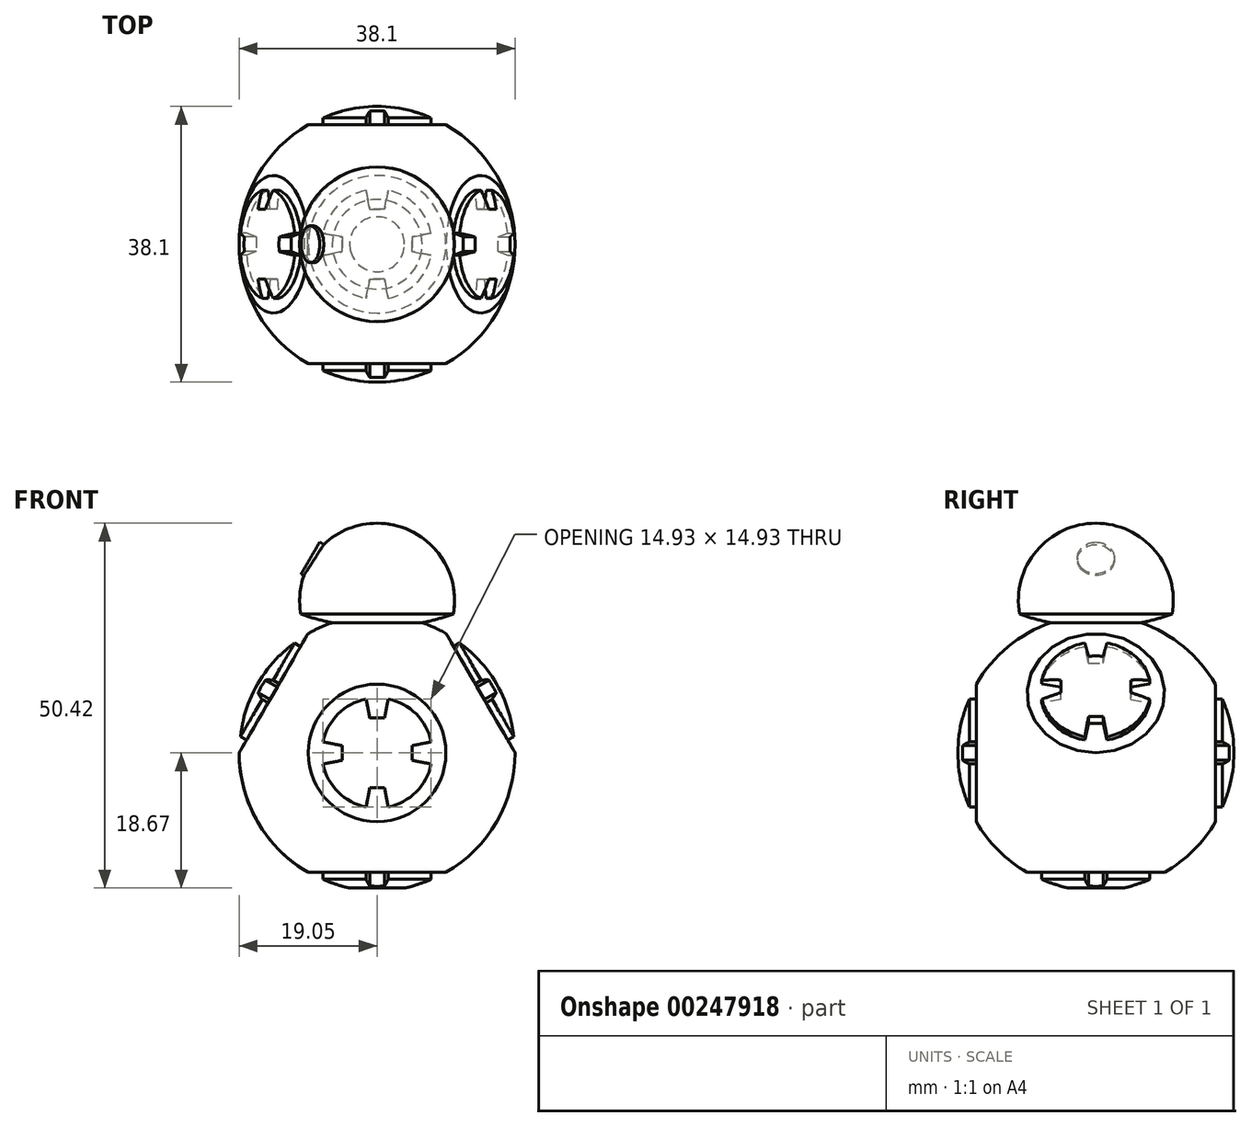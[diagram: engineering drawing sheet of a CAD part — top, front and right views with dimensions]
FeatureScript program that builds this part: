
annotation { "Feature Type Name" : "Feature", "Feature Type Description" : "" }
export const myFeature = defineFeature(function(context is Context, id is Id, definition is map)
    precondition{}
    {
        {
            var Q0;
            Q0=qCreatedBy(makeId("Front.planeOp"),FACE);
            var sketch = newSketch(context, id + "F0", { "sketchPlane" : qUnion([Q0])});
            skArc(sketch, "E0", {"start": v(-6.2, 18.01) * mm, "mid": v(-18.79, -3.15) * mm, "end": v(0, -19.05) * mm});
            skLineSegment(sketch, "E1", {"start": v(0, -19.05) * mm, "end": v(0, 31.75) * mm});
            skArc(sketch, "E2", {"start": v(-10.54, 19.2) * mm, "mid": v(-8.4, 18.52) * mm, "end": v(-6.2, 18.01) * mm});
            skArc(sketch, "E3.trimOffspring", {"start": v(0, 31.75) * mm, "mid": v(-8.2, 27.93) * mm, "end": v(-10.54, 19.2) * mm});
            skPoint(sketch, "E4.trimOffspring.end.orphan", {"position": v(9.8, 19.2) * mm});
            skPoint(sketch, "E5", {"position": v(-17, -8.58) * mm});
            skLineSegment(sketch, "E6", {"start": v(-6, 29.9) * mm, "end": v(-10.66, 21.92) * mm, "construction": true});
            skSolve(sketch);
        }
        {
            var Q0;
            {var subQ0=sQuery(id+"F0.wireOp",EDGE,"E0");Q0=makeQuery(id+"F0.imprint","IMPRINT",FACE,{"disambiguationData":[TD([[makeQuery(id+"F0.imprint","IMPRINT",EDGE,{"derivedFrom":subQ0}),1.0]])]});}
            var Q1;
            Q1=sQuery(id+"F0.wireOp",EDGE,"E1");
            revolve(context, id + "F1", {"entities" : qUnion([Q0]), "axis" : qUnion([Q1]), "revolveType" : RevolveType.FULL});
        }
        {
            var Q0;
            Q0=qCreatedBy(makeId("Front.planeOp"),FACE);
            cPlane(context, id + "F2", {"entities" : qUnion([Q0]), "cplaneType" : CPlaneType.OFFSET, "offset" : 19.05 * mm, "width" : 152.4 * mm, "height" : 152.4 * mm});
        }
        {
            var Q0;
            Q0=qCreatedBy(id+"F2.planeOp",FACE);
            var sketch = newSketch(context, id + "F3", { "sketchPlane" : qUnion([Q0])});
            skCircle(sketch, "E7", {"center": v(0, 0) * mm, "radius": 10.67 * mm});
            skArc(sketch, "E8", {"start": v(1.53, -7.47) * mm, "mid": v(5.39, -5.39) * mm, "end": v(7.47, -1.53) * mm});
            skLineSegment(sketch, "E9", {"start": v(0, -4.83) * mm, "end": v(-1.02, -4.83) * mm});
            skLineSegment(sketch, "E10", {"start": v(-1.02, -4.83) * mm, "end": v(-1.53, -7.47) * mm});
            skLineSegment(sketch, "E11.MirrorCS", {"start": v(1.02, -4.83) * mm, "end": v(1.53, -7.47) * mm});
            skLineSegment(sketch, "E12.MirrorCS", {"start": v(0, -4.83) * mm, "end": v(1.02, -4.83) * mm});
            skLineSegment(sketch, "E13.1.0", {"start": v(4.83, -1.02) * mm, "end": v(7.47, -1.53) * mm});
            skLineSegment(sketch, "E13.1.1", {"start": v(4.83, 0) * mm, "end": v(4.83, 1.02) * mm});
            skLineSegment(sketch, "E13.1.2", {"start": v(4.83, 0) * mm, "end": v(4.83, -1.02) * mm});
            skLineSegment(sketch, "E13.1.3", {"start": v(4.83, 1.02) * mm, "end": v(7.47, 1.53) * mm});
            skLineSegment(sketch, "E13.2.0", {"start": v(1.02, 4.83) * mm, "end": v(1.53, 7.47) * mm});
            skLineSegment(sketch, "E13.2.1", {"start": v(0, 4.83) * mm, "end": v(-1.02, 4.83) * mm});
            skLineSegment(sketch, "E13.2.2", {"start": v(0, 4.83) * mm, "end": v(1.02, 4.83) * mm});
            skLineSegment(sketch, "E13.2.3", {"start": v(-1.02, 4.83) * mm, "end": v(-1.53, 7.47) * mm});
            skLineSegment(sketch, "E13.3.0", {"start": v(-4.83, 1.02) * mm, "end": v(-7.47, 1.53) * mm});
            skLineSegment(sketch, "E13.3.1", {"start": v(-4.83, 0) * mm, "end": v(-4.83, -1.02) * mm});
            skLineSegment(sketch, "E13.3.2", {"start": v(-4.83, 0) * mm, "end": v(-4.83, 1.02) * mm});
            skLineSegment(sketch, "E13.3.3", {"start": v(-4.83, -1.02) * mm, "end": v(-7.47, -1.53) * mm});
            skArc(sketch, "E14.trimOffspring", {"start": v(-7.47, -1.53) * mm, "mid": v(-5.39, -5.39) * mm, "end": v(-1.53, -7.47) * mm});
            skArc(sketch, "E15.trimOffspring", {"start": v(-1.53, 7.47) * mm, "mid": v(-5.39, 5.39) * mm, "end": v(-7.47, 1.53) * mm});
            skArc(sketch, "E16.trimOffspring", {"start": v(7.47, 1.53) * mm, "mid": v(5.39, 5.39) * mm, "end": v(1.53, 7.47) * mm});
            skSolve(sketch);
        }
        {
            var Q0;
            Q0 = qSketchRegion(id + "F3", true);
            extrude(context, id + "F4", {"entities" : qUnion([Q0]), "operationType" : NewBodyOperationType.REMOVE, "oppositeDirection" : true, "depth" : 2.54 * mm});
        }
        {
            var Q0;
            Q0=qCreatedBy(makeId("Front.planeOp"),FACE);
            var sketch = newSketch(context, id + "F5", { "sketchPlane" : qUnion([Q0])});
            skCircle(sketch, "E17", {"center": v(0, 0) * mm, "radius": 19.05 * mm});
            skLineSegment(sketch, "E18", {"start": v(0, -19.05) * mm, "end": v(0, 19.05) * mm});
            skLineSegment(sketch, "E19", {"start": v(0, 0) * mm, "end": v(0, 19.05) * mm});
            skLineSegment(sketch, "E20", {"start": v(0, 19.05) * mm, "end": v(16.5, -9.53) * mm});
            skLineSegment(sketch, "E21", {"start": v(16.5, -9.53) * mm, "end": v(0, -9.53) * mm});
            skLineSegment(sketch, "E22.MirrorCS", {"start": v(0, 19.05) * mm, "end": v(-16.5, -9.53) * mm});
            skLineSegment(sketch, "E23.MirrorCS", {"start": v(-16.5, -9.53) * mm, "end": v(0, -9.53) * mm});
            skLineSegment(sketch, "E24", {"start": v(16.5, 9.53) * mm, "end": v(25.5, -6.07) * mm});
            skLineSegment(sketch, "E25.MirrorCS", {"start": v(16.5, 9.52) * mm, "end": v(7.5, 25.12) * mm});
            skLineSegment(sketch, "E26.1.0", {"start": v(-16.5, 9.53) * mm, "end": v(-25.5, -6.07) * mm});
            skLineSegment(sketch, "E26.1.1", {"start": v(-16.5, 9.52) * mm, "end": v(-7.5, 25.12) * mm});
            skLineSegment(sketch, "E26.2.0", {"start": v(0, -19.05) * mm, "end": v(18, -19.05) * mm});
            skLineSegment(sketch, "E26.2.1", {"start": v(0, -19.05) * mm, "end": v(-18, -19.05) * mm});
            skPoint(sketch, "E27.start.orphan", {"position": v(8.25, 4.76) * mm});
            skLineSegment(sketch, "E28", {"start": v(0, 0) * mm, "end": v(-16.5, 9.53) * mm});
            skLineSegment(sketch, "E29", {"start": v(0, 0) * mm, "end": v(16.5, 9.53) * mm});
            skSolve(sketch);
        }
        {
            var Q0;
            Q0=sQuery(id+"F5.wireOp",VERTEX,"E26.2.0.start");
            var Q1;
            Q1=sQuery(id+"F5.wireOp",EDGE,"E18");
            cPlane(context, id + "F6", {"entities" : qUnion([Q0, Q1]), "cplaneType" : CPlaneType.LINE_POINT, "offset" : 25.4 * mm, "width" : 152.4 * mm, "height" : 152.4 * mm});
        }
        {
            var Q0;
            Q0=qCreatedBy(id+"F6.planeOp",FACE);
            var sketch = newSketch(context, id + "F7", { "sketchPlane" : qUnion([Q0])});
            skCircle(sketch, "E30", {"center": v(0, 0) * mm, "radius": 10.67 * mm});
            skArc(sketch, "E31", {"start": v(1.53, -7.47) * mm, "mid": v(5.39, -5.39) * mm, "end": v(7.47, -1.53) * mm});
            skLineSegment(sketch, "E32", {"start": v(0, -4.83) * mm, "end": v(-1.02, -4.83) * mm});
            skLineSegment(sketch, "E33", {"start": v(-1.02, -4.83) * mm, "end": v(-1.53, -7.47) * mm});
            skLineSegment(sketch, "E34.MirrorCS", {"start": v(1.02, -4.83) * mm, "end": v(1.53, -7.47) * mm});
            skLineSegment(sketch, "E35.MirrorCS", {"start": v(0, -4.83) * mm, "end": v(1.02, -4.83) * mm});
            skLineSegment(sketch, "E36.1.0", {"start": v(4.83, -1.02) * mm, "end": v(7.47, -1.53) * mm});
            skLineSegment(sketch, "E36.1.1", {"start": v(4.83, 0) * mm, "end": v(4.83, 1.02) * mm});
            skLineSegment(sketch, "E36.1.2", {"start": v(4.83, 0) * mm, "end": v(4.83, -1.02) * mm});
            skLineSegment(sketch, "E36.1.3", {"start": v(4.83, 1.02) * mm, "end": v(7.47, 1.53) * mm});
            skLineSegment(sketch, "E36.2.0", {"start": v(1.02, 4.83) * mm, "end": v(1.53, 7.47) * mm});
            skLineSegment(sketch, "E36.2.1", {"start": v(0, 4.83) * mm, "end": v(-1.02, 4.83) * mm});
            skLineSegment(sketch, "E36.2.2", {"start": v(0, 4.83) * mm, "end": v(1.02, 4.83) * mm});
            skLineSegment(sketch, "E36.2.3", {"start": v(-1.02, 4.83) * mm, "end": v(-1.53, 7.47) * mm});
            skLineSegment(sketch, "E36.3.0", {"start": v(-4.83, 1.02) * mm, "end": v(-7.47, 1.53) * mm});
            skLineSegment(sketch, "E36.3.1", {"start": v(-4.83, 0) * mm, "end": v(-4.83, -1.02) * mm});
            skLineSegment(sketch, "E36.3.2", {"start": v(-4.83, 0) * mm, "end": v(-4.83, 1.02) * mm});
            skLineSegment(sketch, "E36.3.3", {"start": v(-4.83, -1.02) * mm, "end": v(-7.47, -1.53) * mm});
            skArc(sketch, "E37.trimOffspring", {"start": v(-7.47, -1.53) * mm, "mid": v(-5.39, -5.39) * mm, "end": v(-1.53, -7.47) * mm});
            skArc(sketch, "E38.trimOffspring", {"start": v(-1.53, 7.47) * mm, "mid": v(-5.39, 5.39) * mm, "end": v(-7.47, 1.53) * mm});
            skArc(sketch, "E39.trimOffspring", {"start": v(7.47, 1.53) * mm, "mid": v(5.39, 5.39) * mm, "end": v(1.53, 7.47) * mm});
            skSolve(sketch);
        }
        {
            var Q0;
            Q0=makeQuery(id+"F7.imprint","IMPRINT",FACE,{"disambiguationData":[TD([[makeQuery(id+"F7.imprint","IMPRINT",EDGE,{"derivedFrom":sQuery(id+"F7.wireOp",EDGE,"E30")}),1.0]])]});
            extrude(context, id + "F8", {"entities" : qUnion([Q0]), "operationType" : NewBodyOperationType.REMOVE, "depth" : 2.54 * mm});
        }
        {
            var Q0;
            Q0=sQuery(id+"F5.wireOp",VERTEX,"E28.end");
            var Q1;
            Q1=sQuery(id+"F5.wireOp",EDGE,"E28");
            cPlane(context, id + "F9", {"entities" : qUnion([Q0, Q1]), "cplaneType" : CPlaneType.LINE_POINT, "offset" : 25.4 * mm, "width" : 152.4 * mm, "height" : 152.4 * mm});
        }
        {
            var Q0;
            Q0=qCreatedBy(id+"F9.planeOp",FACE);
            var sketch = newSketch(context, id + "F10", { "sketchPlane" : qUnion([Q0])});
            skCircle(sketch, "E40", {"center": v(0, 0) * mm, "radius": 10.67 * mm});
            skArc(sketch, "E41", {"start": v(1.53, -7.47) * mm, "mid": v(5.39, -5.39) * mm, "end": v(7.47, -1.53) * mm});
            skLineSegment(sketch, "E42", {"start": v(0, -4.83) * mm, "end": v(-1.02, -4.83) * mm});
            skLineSegment(sketch, "E43", {"start": v(-1.02, -4.83) * mm, "end": v(-1.53, -7.47) * mm});
            skLineSegment(sketch, "E44.MirrorCS", {"start": v(1.02, -4.83) * mm, "end": v(1.53, -7.47) * mm});
            skLineSegment(sketch, "E45.MirrorCS", {"start": v(0, -4.83) * mm, "end": v(1.02, -4.83) * mm});
            skLineSegment(sketch, "E46.1.0", {"start": v(4.83, -1.02) * mm, "end": v(7.47, -1.53) * mm});
            skLineSegment(sketch, "E46.1.1", {"start": v(4.83, 0) * mm, "end": v(4.83, 1.02) * mm});
            skLineSegment(sketch, "E46.1.2", {"start": v(4.83, 0) * mm, "end": v(4.83, -1.02) * mm});
            skLineSegment(sketch, "E46.1.3", {"start": v(4.83, 1.02) * mm, "end": v(7.47, 1.53) * mm});
            skLineSegment(sketch, "E46.2.0", {"start": v(1.02, 4.83) * mm, "end": v(1.53, 7.47) * mm});
            skLineSegment(sketch, "E46.2.1", {"start": v(0, 4.83) * mm, "end": v(-1.02, 4.83) * mm});
            skLineSegment(sketch, "E46.2.2", {"start": v(0, 4.83) * mm, "end": v(1.02, 4.83) * mm});
            skLineSegment(sketch, "E46.2.3", {"start": v(-1.02, 4.83) * mm, "end": v(-1.53, 7.47) * mm});
            skLineSegment(sketch, "E46.3.0", {"start": v(-4.83, 1.02) * mm, "end": v(-7.47, 1.53) * mm});
            skLineSegment(sketch, "E46.3.1", {"start": v(-4.83, 0) * mm, "end": v(-4.83, -1.02) * mm});
            skLineSegment(sketch, "E46.3.2", {"start": v(-4.83, 0) * mm, "end": v(-4.83, 1.02) * mm});
            skLineSegment(sketch, "E46.3.3", {"start": v(-4.83, -1.02) * mm, "end": v(-7.47, -1.53) * mm});
            skArc(sketch, "E47.trimOffspring", {"start": v(-7.47, -1.53) * mm, "mid": v(-5.39, -5.39) * mm, "end": v(-1.53, -7.47) * mm});
            skArc(sketch, "E48.trimOffspring", {"start": v(-1.53, 7.47) * mm, "mid": v(-5.39, 5.39) * mm, "end": v(-7.47, 1.53) * mm});
            skArc(sketch, "E49.trimOffspring", {"start": v(7.47, 1.53) * mm, "mid": v(5.39, 5.39) * mm, "end": v(1.53, 7.47) * mm});
            skSolve(sketch);
        }
        {
            var Q0;
            Q0=makeQuery(id+"F10.imprint","IMPRINT",FACE,{"disambiguationData":[TD([[makeQuery(id+"F10.imprint","IMPRINT",EDGE,{"derivedFrom":sQuery(id+"F10.wireOp",EDGE,"E40")}),1.0]])]});
            extrude(context, id + "F11", {"entities" : qUnion([Q0]), "operationType" : NewBodyOperationType.REMOVE, "oppositeDirection" : true, "depth" : 2.54 * mm});
        }
        {
            var Q0;
            Q0=sQuery(id+"F5.wireOp",VERTEX,"E29.end");
            var Q1;
            Q1=sQuery(id+"F5.wireOp",EDGE,"E29");
            cPlane(context, id + "F12", {"entities" : qUnion([Q0, Q1]), "cplaneType" : CPlaneType.LINE_POINT, "offset" : 25.4 * mm, "width" : 152.4 * mm, "height" : 152.4 * mm});
        }
        {
            var Q0;
            Q0=qCreatedBy(id+"F12.planeOp",FACE);
            var sketch = newSketch(context, id + "F13", { "sketchPlane" : qUnion([Q0])});
            skCircle(sketch, "E50", {"center": v(0, 0) * mm, "radius": 10.67 * mm});
            skArc(sketch, "E51", {"start": v(1.53, -7.47) * mm, "mid": v(5.39, -5.39) * mm, "end": v(7.47, -1.53) * mm});
            skLineSegment(sketch, "E52", {"start": v(0, -4.83) * mm, "end": v(-1.02, -4.83) * mm});
            skLineSegment(sketch, "E53", {"start": v(-1.02, -4.83) * mm, "end": v(-1.53, -7.47) * mm});
            skLineSegment(sketch, "E54.MirrorCS", {"start": v(1.02, -4.83) * mm, "end": v(1.53, -7.47) * mm});
            skLineSegment(sketch, "E55.MirrorCS", {"start": v(0, -4.83) * mm, "end": v(1.02, -4.83) * mm});
            skLineSegment(sketch, "E56.1.0", {"start": v(4.83, -1.02) * mm, "end": v(7.47, -1.53) * mm});
            skLineSegment(sketch, "E56.1.1", {"start": v(4.83, 0) * mm, "end": v(4.83, 1.02) * mm});
            skLineSegment(sketch, "E56.1.2", {"start": v(4.83, 0) * mm, "end": v(4.83, -1.02) * mm});
            skLineSegment(sketch, "E56.1.3", {"start": v(4.83, 1.02) * mm, "end": v(7.47, 1.53) * mm});
            skLineSegment(sketch, "E56.2.0", {"start": v(1.02, 4.83) * mm, "end": v(1.53, 7.47) * mm});
            skLineSegment(sketch, "E56.2.1", {"start": v(0, 4.83) * mm, "end": v(-1.02, 4.83) * mm});
            skLineSegment(sketch, "E56.2.2", {"start": v(0, 4.83) * mm, "end": v(1.02, 4.83) * mm});
            skLineSegment(sketch, "E56.2.3", {"start": v(-1.02, 4.83) * mm, "end": v(-1.53, 7.47) * mm});
            skLineSegment(sketch, "E56.3.0", {"start": v(-4.83, 1.02) * mm, "end": v(-7.47, 1.53) * mm});
            skLineSegment(sketch, "E56.3.1", {"start": v(-4.83, 0) * mm, "end": v(-4.83, -1.02) * mm});
            skLineSegment(sketch, "E56.3.2", {"start": v(-4.83, 0) * mm, "end": v(-4.83, 1.02) * mm});
            skLineSegment(sketch, "E56.3.3", {"start": v(-4.83, -1.02) * mm, "end": v(-7.47, -1.53) * mm});
            skArc(sketch, "E57.trimOffspring", {"start": v(-7.47, -1.53) * mm, "mid": v(-5.39, -5.39) * mm, "end": v(-1.53, -7.47) * mm});
            skArc(sketch, "E58.trimOffspring", {"start": v(-1.53, 7.47) * mm, "mid": v(-5.39, 5.39) * mm, "end": v(-7.47, 1.53) * mm});
            skArc(sketch, "E59.trimOffspring", {"start": v(7.47, 1.53) * mm, "mid": v(5.39, 5.39) * mm, "end": v(1.53, 7.47) * mm});
            skSolve(sketch);
        }
        {
            var Q0;
            Q0=makeQuery(id+"F13.imprint","IMPRINT",FACE,{"disambiguationData":[TD([[makeQuery(id+"F13.imprint","IMPRINT",EDGE,{"derivedFrom":sQuery(id+"F13.wireOp",EDGE,"E50")}),1.0]])]});
            extrude(context, id + "F14", {"entities" : qUnion([Q0]), "operationType" : NewBodyOperationType.REMOVE, "oppositeDirection" : true, "depth" : 2.54 * mm});
        }
        {
            var Q0;
            Q0=qCreatedBy(makeId("Right.planeOp"),FACE);
            var sketch = newSketch(context, id + "F15", { "sketchPlane" : qUnion([Q0])});
            skCircle(sketch, "E60", {"center": v(0, 0) * mm, "radius": 19.05 * mm});
            skLineSegment(sketch, "E61", {"start": v(0, 0) * mm, "end": v(19.05, 0) * mm});
            skSolve(sketch);
        }
        {
            var Q0;
            Q0=sQuery(id+"F15.wireOp",VERTEX,"E61.end");
            var Q1;
            Q1=sQuery(id+"F15.wireOp",EDGE,"E61");
            cPlane(context, id + "F16", {"entities" : qUnion([Q0, Q1]), "cplaneType" : CPlaneType.LINE_POINT, "offset" : 25.4 * mm, "width" : 152.4 * mm, "height" : 152.4 * mm});
        }
        {
            var Q0;
            Q0=qCreatedBy(id+"F16.planeOp",FACE);
            var sketch = newSketch(context, id + "F17", { "sketchPlane" : qUnion([Q0])});
            skCircle(sketch, "E62", {"center": v(0, 0) * mm, "radius": 10.67 * mm});
            skArc(sketch, "E63", {"start": v(1.53, -7.47) * mm, "mid": v(5.39, -5.39) * mm, "end": v(7.47, -1.53) * mm});
            skLineSegment(sketch, "E64", {"start": v(0, -4.83) * mm, "end": v(-1.02, -4.83) * mm});
            skLineSegment(sketch, "E65", {"start": v(-1.02, -4.83) * mm, "end": v(-1.53, -7.47) * mm});
            skLineSegment(sketch, "E66.MirrorCS", {"start": v(1.02, -4.83) * mm, "end": v(1.53, -7.47) * mm});
            skLineSegment(sketch, "E67.MirrorCS", {"start": v(0, -4.83) * mm, "end": v(1.02, -4.83) * mm});
            skLineSegment(sketch, "E68.1.0", {"start": v(4.83, -1.02) * mm, "end": v(7.47, -1.53) * mm});
            skLineSegment(sketch, "E68.1.1", {"start": v(4.83, 0) * mm, "end": v(4.83, 1.02) * mm});
            skLineSegment(sketch, "E68.1.2", {"start": v(4.83, 0) * mm, "end": v(4.83, -1.02) * mm});
            skLineSegment(sketch, "E68.1.3", {"start": v(4.83, 1.02) * mm, "end": v(7.47, 1.53) * mm});
            skLineSegment(sketch, "E68.2.0", {"start": v(1.02, 4.83) * mm, "end": v(1.53, 7.47) * mm});
            skLineSegment(sketch, "E68.2.1", {"start": v(0, 4.83) * mm, "end": v(-1.02, 4.83) * mm});
            skLineSegment(sketch, "E68.2.2", {"start": v(0, 4.83) * mm, "end": v(1.02, 4.83) * mm});
            skLineSegment(sketch, "E68.2.3", {"start": v(-1.02, 4.83) * mm, "end": v(-1.53, 7.47) * mm});
            skLineSegment(sketch, "E68.3.0", {"start": v(-4.83, 1.02) * mm, "end": v(-7.47, 1.53) * mm});
            skLineSegment(sketch, "E68.3.1", {"start": v(-4.83, 0) * mm, "end": v(-4.83, -1.02) * mm});
            skLineSegment(sketch, "E68.3.2", {"start": v(-4.83, 0) * mm, "end": v(-4.83, 1.02) * mm});
            skLineSegment(sketch, "E68.3.3", {"start": v(-4.83, -1.02) * mm, "end": v(-7.47, -1.53) * mm});
            skArc(sketch, "E69.trimOffspring", {"start": v(-7.47, -1.53) * mm, "mid": v(-5.39, -5.39) * mm, "end": v(-1.53, -7.47) * mm});
            skArc(sketch, "E70.trimOffspring", {"start": v(-1.53, 7.47) * mm, "mid": v(-5.39, 5.39) * mm, "end": v(-7.47, 1.53) * mm});
            skArc(sketch, "E71.trimOffspring", {"start": v(7.47, 1.53) * mm, "mid": v(5.39, 5.39) * mm, "end": v(1.53, 7.47) * mm});
            skSolve(sketch);
        }
        {
            var Q0;
            Q0=makeQuery(id+"F17.imprint","IMPRINT",FACE,{"disambiguationData":[TD([[makeQuery(id+"F17.imprint","IMPRINT",EDGE,{"derivedFrom":sQuery(id+"F17.wireOp",EDGE,"E62")}),1.0]])]});
            extrude(context, id + "F18", {"entities" : qUnion([Q0]), "operationType" : NewBodyOperationType.REMOVE, "oppositeDirection" : true, "depth" : 2.54 * mm});
        }
        {
            var Q0;
            Q0=sQuery(id+"F0.wireOp",EDGE,"E6");
            cPlane(context, id + "F19", {"entities" : qUnion([Q0]), "cplaneType" : CPlaneType.LINE_ANGLE, "offset" : 25.4 * mm, "angle" : 0 * degree, "flipAlignment" : true, "width" : 152.4 * mm, "height" : 152.4 * mm});
        }
        {
            var Q0;
            Q0=qCreatedBy(id+"F19.planeOp",FACE);
            var sketch = newSketch(context, id + "F20", { "sketchPlane" : qUnion([Q0])});
            skCircle(sketch, "E72", {"center": v(0, 18.64) * mm, "radius": 2.54 * mm});
            skSolve(sketch);
        }
        {
            var Q0;
            Q0 = qSketchRegion(id + "F20", true);
            var Q1;
            Q1=sQuery(id+"F20.wireOp",EDGE,"E72");
            extrude(context, id + "F21", {"entities" : qUnion([Q0]), "operationType" : NewBodyOperationType.ADD, "surfaceEntities" : qUnion([Q1]), "depth" : 1.27 * mm});
        }
        {
            var Q0;
            Q0=qCreatedBy(id+"F6.planeOp",FACE);
            var sketch = newSketch(context, id + "F22", { "sketchPlane" : qUnion([Q0])});
            skCircle(sketch, "E73", {"center": v(0, 0) * mm, "radius": 3.81 * mm});
            skSolve(sketch);
        }
        {
            var Q0;
            Q0 = qSketchRegion(id + "F22", true);
            extrude(context, id + "F23", {"entities" : qUnion([Q0]), "operationType" : NewBodyOperationType.REMOVE, "depth" : 0.38 * mm});
        }
    });
